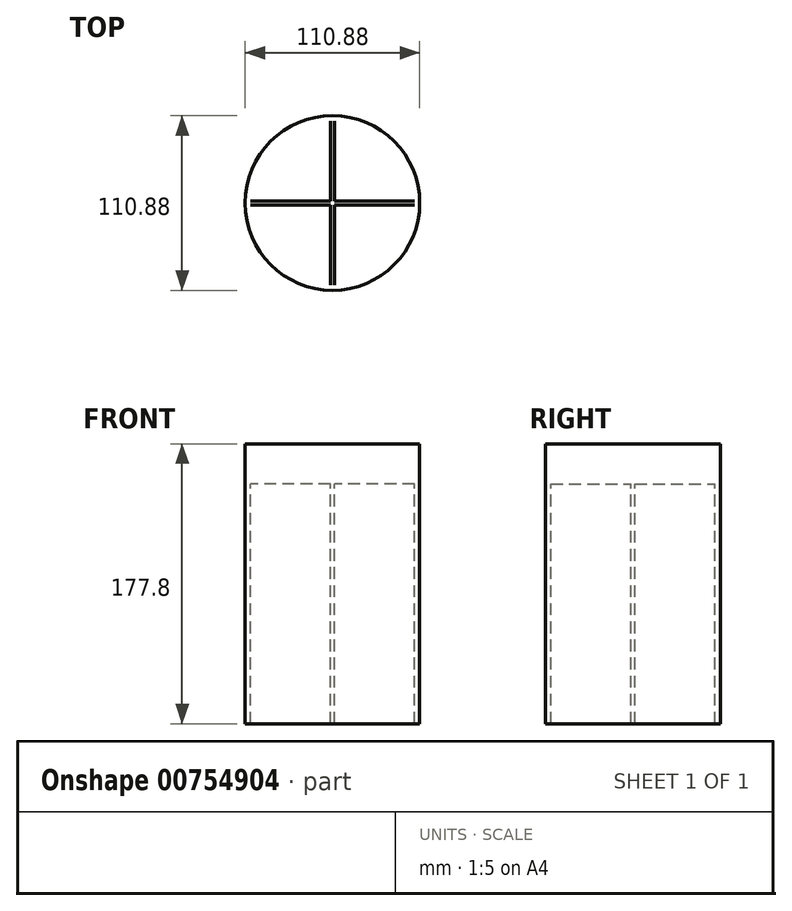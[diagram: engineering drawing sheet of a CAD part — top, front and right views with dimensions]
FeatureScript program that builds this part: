
annotation { "Feature Type Name" : "Feature", "Feature Type Description" : "" }
export const myFeature = defineFeature(function(context is Context, id is Id, definition is map)
    precondition{}
    {
        {
            var Q0;
            Q0=qCreatedBy(makeId("Top.planeOp"),FACE);
            var sketch = newSketch(context, id + "F0", { "sketchPlane" : qUnion([Q0])});
            skLineSegment(sketch, "E0", {"start": v(-1.27, -1.15) * mm, "end": v(-52.07, -1.15) * mm});
            skLineSegment(sketch, "E1", {"start": v(-1.27, 1.15) * mm, "end": v(-52.07, 1.15) * mm});
            skLineSegment(sketch, "E2", {"start": v(-1.27, 1.15) * mm, "end": v(-1.27, 51.95) * mm});
            skLineSegment(sketch, "E3", {"start": v(1.2, 1.25) * mm, "end": v(1.2, 52.05) * mm});
            skLineSegment(sketch, "E4", {"start": v(52.03, 1.13) * mm, "end": v(1.23, 1.13) * mm});
            skLineSegment(sketch, "E5", {"start": v(1.23, -51.95) * mm, "end": v(1.23, -1.15) * mm});
            skLineSegment(sketch, "E6", {"start": v(52.03, -1.15) * mm, "end": v(1.23, -1.15) * mm});
            skLineSegment(sketch, "E7", {"start": v(-1.27, -52.01) * mm, "end": v(-1.27, -1.21) * mm});
            skSolve(sketch);
        }
        {
            var Q0;
            Q0=sQuery(id+"F0.wireOp",EDGE,"E1");
            var Q1;
            Q1=sQuery(id+"F0.wireOp",EDGE,"E2");
            var Q2;
            Q2=sQuery(id+"F0.wireOp",EDGE,"E3");
            var Q3;
            Q3=sQuery(id+"F0.wireOp",EDGE,"E4");
            var Q4;
            Q4=sQuery(id+"F0.wireOp",EDGE,"E6");
            var Q5;
            Q5=sQuery(id+"F0.wireOp",EDGE,"E5");
            var Q6;
            Q6=sQuery(id+"F0.wireOp",EDGE,"E7");
            var Q7;
            Q7=sQuery(id+"F0.wireOp",EDGE,"E0");
            extrude(context, id + "F1", {"bodyType" : ToolBodyType.SURFACE, "surfaceEntities" : qUnion([Q0, Q1, Q2, Q3, Q4, Q5, Q6, Q7]), "depth" : 152.4 * mm, "offsetDistance" : 25.4 * mm});
        }
        {
            var Q0;
            Q0=qCreatedBy(makeId("Top.planeOp"),FACE);
            var sketch = newSketch(context, id + "F2", { "sketchPlane" : qUnion([Q0])});
            skCircle(sketch, "E8", {"center": v(0, 0) * mm, "radius": 55.44 * mm});
            skSolve(sketch);
        }
        {
            var Q0;
            Q0=sQuery(id+"F2.wireOp",EDGE,"E8");
            extrude(context, id + "F3", {"bodyType" : ToolBodyType.SURFACE, "surfaceEntities" : qUnion([Q0]), "depth" : 177.8 * mm, "offsetDistance" : 25.4 * mm});
        }
    });
